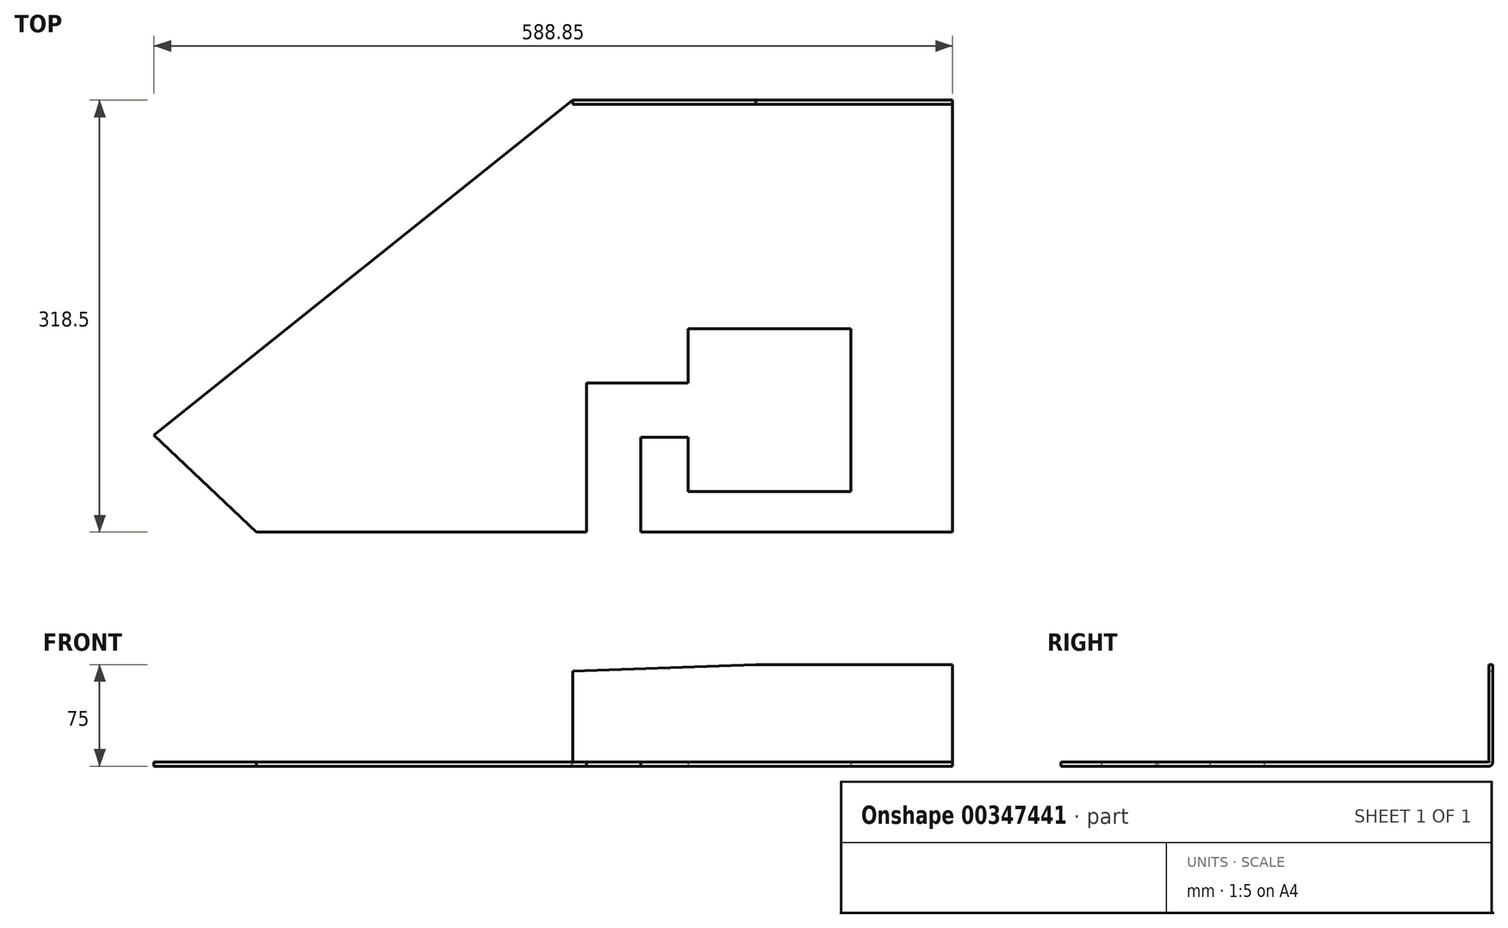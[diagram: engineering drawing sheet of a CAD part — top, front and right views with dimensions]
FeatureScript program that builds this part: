
annotation { "Feature Type Name" : "Feature", "Feature Type Description" : "" }
export const myFeature = defineFeature(function(context is Context, id is Id, definition is map)
    precondition{}
    {
        {
            var Q0;
            Q0=qCreatedBy(makeId("Top.planeOp"),FACE);
            var sketch = newSketch(context, id + "F0", { "sketchPlane" : qUnion([Q0])});
            skLineSegment(sketch, "E0", {"start": v(0, 0) * mm, "end": v(-230, 0) * mm});
            skLineSegment(sketch, "E1", {"start": v(-230, 0) * mm, "end": v(-230, 70) * mm});
            skLineSegment(sketch, "E2", {"start": v(-230, 70) * mm, "end": v(-195, 70) * mm});
            skLineSegment(sketch, "E3", {"start": v(-195, 70) * mm, "end": v(-195, 30) * mm});
            skLineSegment(sketch, "E4", {"start": v(-195, 30) * mm, "end": v(-75, 30) * mm});
            skLineSegment(sketch, "E5", {"start": v(-75, 30) * mm, "end": v(-75, 150) * mm});
            skLineSegment(sketch, "E6", {"start": v(-75, 150) * mm, "end": v(-195, 150) * mm});
            skLineSegment(sketch, "E7", {"start": v(-195, 150) * mm, "end": v(-195, 110) * mm});
            skLineSegment(sketch, "E8", {"start": v(-195, 110) * mm, "end": v(-270, 110) * mm});
            skLineSegment(sketch, "E9", {"start": v(-270, 110) * mm, "end": v(-270, 0) * mm});
            skLineSegment(sketch, "E10", {"start": v(-270, 0) * mm, "end": v(-513.5, 0) * mm});
            skLineSegment(sketch, "E11", {"start": v(-513.5, 0) * mm, "end": v(-588.85, 71.5) * mm});
            skLineSegment(sketch, "E12", {"start": v(-588.85, 71.5) * mm, "end": v(-280, 318.5) * mm});
            skLineSegment(sketch, "E13", {"start": v(-280, 318.5) * mm, "end": v(0, 318.5) * mm});
            skLineSegment(sketch, "E14", {"start": v(0, 318.5) * mm, "end": v(0, 0) * mm});
            skSolve(sketch);
        }
        {
            var Q0;
            Q0=makeQuery(id+"F0.imprint","IMPRINT",FACE,{"disambiguationData":[TD([[makeQuery(id+"F0.imprint","IMPRINT",EDGE,{"derivedFrom":sQuery(id+"F0.wireOp",EDGE,"E0")}),-1.0]])]});
            extrude(context, id + "F1", {"entities" : qUnion([Q0]), "depth" : 3 * mm});
        }
        {
            var Q0;
            Q0=makeQuery(id+"F1.opExtrude","SWEPT_FACE",FACE,{"disambiguationData":[OSD([sQuery(id+"F0.wireOp",EDGE,"E13")])]});
            var sketch = newSketch(context, id + "F2", { "sketchPlane" : qUnion([Q0])});
            skLineSegment(sketch, "E15", {"start": v(0, 3) * mm, "end": v(0, 75) * mm});
            skLineSegment(sketch, "E16", {"start": v(0, 75) * mm, "end": v(145, 75) * mm});
            skLineSegment(sketch, "E17", {"start": v(280, 70) * mm, "end": v(280, 3) * mm});
            skLineSegment(sketch, "E18", {"start": v(280, 3) * mm, "end": v(0, 3) * mm});
            skLineSegment(sketch, "E19", {"start": v(145, 75) * mm, "end": v(280, 70) * mm});
            skPoint(sketch, "E20.orphan", {"position": v(280, 75) * mm});
            skSolve(sketch);
        }
        {
            var Q0;
            Q0=makeQuery(id+"F2.imprint","IMPRINT",FACE,{"disambiguationData":[TD([[makeQuery(id+"F2.imprint","IMPRINT",EDGE,{"derivedFrom":sQuery(id+"F2.wireOp",EDGE,"E15")}),-1.0]])]});
            extrude(context, id + "F3", {"entities" : qUnion([Q0]), "operationType" : NewBodyOperationType.ADD, "oppositeDirection" : true, "depth" : 3 * mm});
        }
        {
            var Q0;
            Q0=makeQuery(id+"F3.opExtrude","CAP_EDGE",EDGE,{"disambiguationData":[OSD([sQuery(id+"F2.wireOp",EDGE,"E18")])],"isStart":false});
            var Q1;
            Q1=makeQuery(id+"F1.opExtrude","CAP_EDGE",EDGE,{"disambiguationData":[OSD([sQuery(id+"F0.wireOp",EDGE,"E13")])],"isStart":true});
            fillet(context, id + "F4", {"entities" : qUnion([Q0, Q1]), "radius" : 3 * mm, "tangentPropagation" : true, "allowEdgeOverflow" : false});
        }
    });
